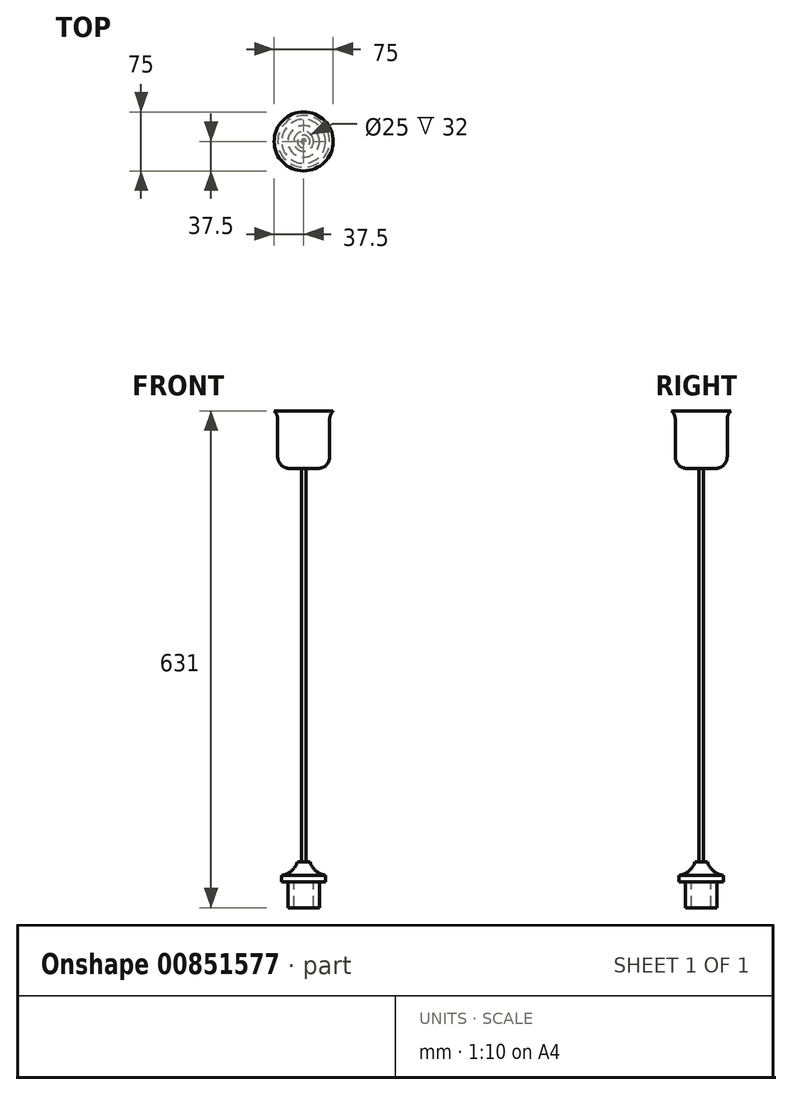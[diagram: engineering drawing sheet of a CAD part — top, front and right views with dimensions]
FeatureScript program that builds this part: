
annotation { "Feature Type Name" : "Feature", "Feature Type Description" : "" }
export const myFeature = defineFeature(function(context is Context, id is Id, definition is map)
    precondition{}
    {
        {
            var Q0;
            Q0=qCreatedBy(makeId("Front.planeOp"),FACE);
            var sketch = newSketch(context, id + "F0", { "sketchPlane" : qUnion([Q0])});
            skLineSegment(sketch, "E0", {"start": v(0, 32) * mm, "end": v(12.5, 32) * mm});
            skLineSegment(sketch, "E1", {"start": v(12.5, 32) * mm, "end": v(12.5, 0) * mm});
            skLineSegment(sketch, "E2", {"start": v(12.5, 0) * mm, "end": v(20, 0) * mm});
            skLineSegment(sketch, "E3", {"start": v(20, 0) * mm, "end": v(20, 33) * mm});
            skLineSegment(sketch, "E4", {"start": v(20, 33) * mm, "end": v(28, 33) * mm});
            skLineSegment(sketch, "E5", {"start": v(28, 33) * mm, "end": v(28, 41) * mm});
            skLineSegment(sketch, "E6", {"start": v(3, 58) * mm, "end": v(8, 58) * mm});
            skLineSegment(sketch, "E7", {"start": v(0, 0) * mm, "end": v(0, 50.45) * mm, "construction": true});
            skArc(sketch, "E8", {"start": v(8, 58) * mm, "mid": v(15.59, 46.66) * mm, "end": v(28, 41) * mm});
            skLineSegment(sketch, "E9", {"start": v(3, 58) * mm, "end": v(3, 558) * mm});
            skLineSegment(sketch, "E10", {"start": v(3, 558) * mm, "end": v(18, 558) * mm});
            skArc(sketch, "E11", {"start": v(18, 558) * mm, "mid": v(28.6, 562.4) * mm, "end": v(33, 573) * mm});
            skLineSegment(sketch, "E12", {"start": v(33, 573) * mm, "end": v(33, 620.29) * mm});
            skLineSegment(sketch, "E13", {"start": v(37.5, 631) * mm, "end": v(0, 631) * mm});
            skLineSegment(sketch, "E14", {"start": v(0, 631) * mm, "end": v(0, 32) * mm});
            skArc(sketch, "E15", {"start": v(37.5, 631) * mm, "mid": v(34.17, 626.1) * mm, "end": v(33, 620.29) * mm});
            skSolve(sketch);
        }
        {
            var Q0;
            Q0=qSketchRegion(id+"F0",true);
            var Q1;
            Q1=sQuery(id+"F0.wireOp",EDGE,"E14");
            revolve(context, id + "F1", {"surfaceOperationType" : NewSurfaceOperationType.NEW, "entities" : qUnion([Q0]), "axis" : qUnion([Q1]), "revolveType" : RevolveType.FULL});
        }
    });
